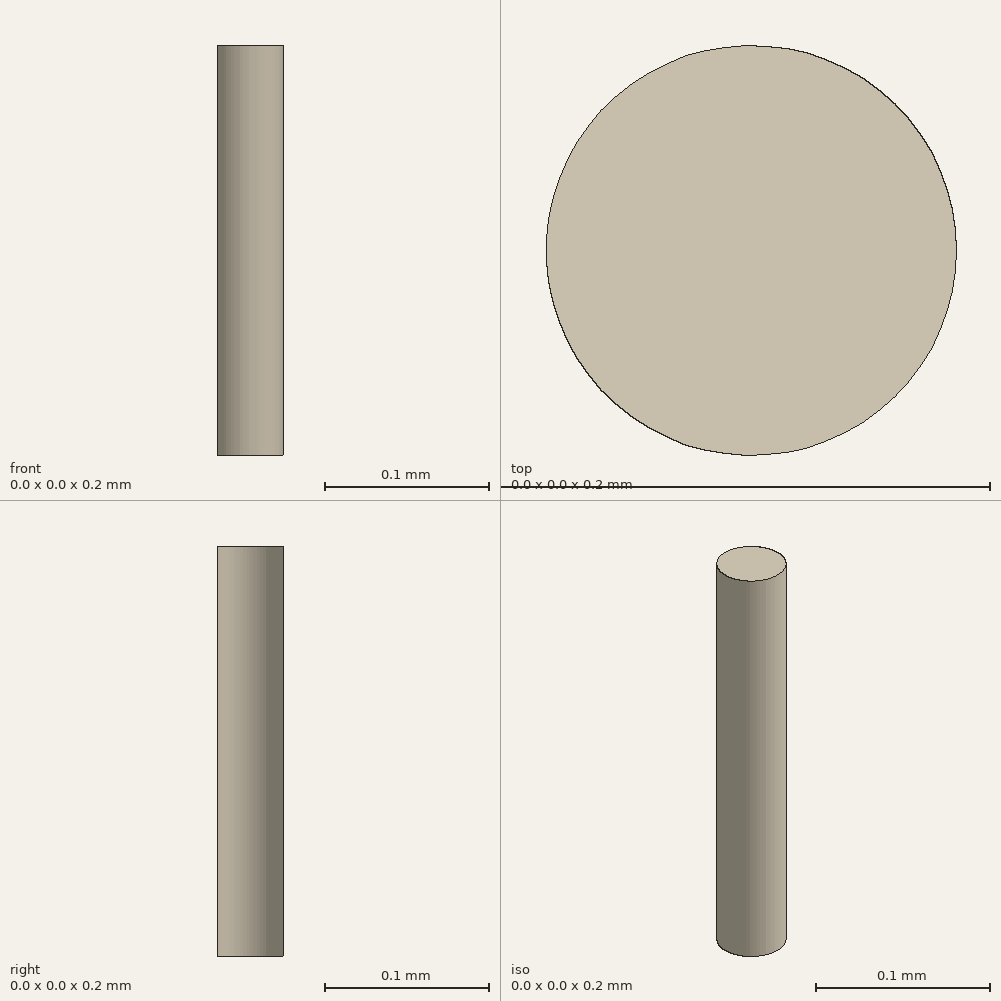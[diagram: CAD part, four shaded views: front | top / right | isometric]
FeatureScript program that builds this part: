
annotation { "Feature Type Name" : "Feature", "Feature Type Description" : "" }
export const myFeature = defineFeature(function(context is Context, id is Id, definition is map)
    precondition{}
    {
        {
            var Q0;
            Q0=qCreatedBy(makeId("Top.planeOp"),FACE);
            var sketch = newSketch(context, id + "F0", { "sketchPlane" : qUnion([Q0])});
            skCircle(sketch, "E0", {"center": v(24.22, -0.45) * mm, "radius": 0.02 * mm});
            skCircle(sketch, "E1", {"center": v(24.22, -0.6) * mm, "radius": 0.02 * mm});
            skCircle(sketch, "E2", {"center": v(24.22, -0.75) * mm, "radius": 0.02 * mm});
            skCircle(sketch, "E3", {"center": v(24.22, -0.3) * mm, "radius": 0.02 * mm});
            skCircle(sketch, "E4", {"center": v(24.22, 0.15) * mm, "radius": 0.02 * mm});
            skCircle(sketch, "E5", {"center": v(24.22, 0) * mm, "radius": 0.02 * mm});
            skCircle(sketch, "E6", {"center": v(24.22, -0.15) * mm, "radius": 0.02 * mm});
            skCircle(sketch, "E7", {"center": v(24.22, 0.75) * mm, "radius": 0.02 * mm});
            skCircle(sketch, "E8", {"center": v(24.22, 0.6) * mm, "radius": 0.02 * mm});
            skCircle(sketch, "E9", {"center": v(24.22, 0.45) * mm, "radius": 0.02 * mm});
            skCircle(sketch, "E10", {"center": v(24.22, 0.3) * mm, "radius": 0.02 * mm});
            skCircle(sketch, "E11", {"center": v(24.33, 0.83) * mm, "radius": 0.03 * mm});
            skCircle(sketch, "E12", {"center": v(24.42, 0.83) * mm, "radius": 0.03 * mm});
            skCircle(sketch, "E13", {"center": v(24.5, 0.83) * mm, "radius": 0.03 * mm});
            skCircle(sketch, "E14", {"center": v(24.59, 0.83) * mm, "radius": 0.03 * mm});
            skCircle(sketch, "E15", {"center": v(24.67, 0.83) * mm, "radius": 0.03 * mm});
            skCircle(sketch, "E16", {"center": v(24.76, 0.83) * mm, "radius": 0.03 * mm});
            skCircle(sketch, "E17", {"center": v(24.1, 0.83) * mm, "radius": 0.03 * mm});
            skCircle(sketch, "E18", {"center": v(24.18, 0.83) * mm, "radius": 0.03 * mm});
            skCircle(sketch, "E19", {"center": v(24.26, 0.83) * mm, "radius": 0.03 * mm});
            skCircle(sketch, "E20", {"center": v(25.3, 0.83) * mm, "radius": 0.03 * mm});
            skCircle(sketch, "E21", {"center": v(25.22, 0.83) * mm, "radius": 0.03 * mm});
            skCircle(sketch, "E22", {"center": v(25.14, 0.83) * mm, "radius": 0.03 * mm});
            skCircle(sketch, "E23", {"center": v(25.05, 0.83) * mm, "radius": 0.03 * mm});
            skCircle(sketch, "E24", {"center": v(24.97, 0.83) * mm, "radius": 0.03 * mm});
            skCircle(sketch, "E25", {"center": v(24.88, 0.83) * mm, "radius": 0.03 * mm});
            skCircle(sketch, "E26", {"center": v(25.53, 0.83) * mm, "radius": 0.03 * mm});
            skCircle(sketch, "E27", {"center": v(25.46, 0.83) * mm, "radius": 0.03 * mm});
            skCircle(sketch, "E28", {"center": v(25.38, 0.83) * mm, "radius": 0.03 * mm});
            skLineSegment(sketch, "E29", {"start": v(24.22, 0.88) * mm, "end": v(22.83, 0.88) * mm});
            skLineSegment(sketch, "E30", {"start": v(24.22, 0.92) * mm, "end": v(22.83, 0.92) * mm});
            skLineSegment(sketch, "E31", {"start": v(22.83, 0.92) * mm, "end": v(22.83, 0.88) * mm});
            skCircle(sketch, "E32", {"center": v(24.29, 0.75) * mm, "radius": 0.03 * mm});
            skCircle(sketch, "E33", {"center": v(24.37, 0.75) * mm, "radius": 0.03 * mm});
            skCircle(sketch, "E34", {"center": v(24.46, 0.75) * mm, "radius": 0.03 * mm});
            skCircle(sketch, "E35", {"center": v(24.54, 0.75) * mm, "radius": 0.03 * mm});
            skCircle(sketch, "E36", {"center": v(24.63, 0.75) * mm, "radius": 0.03 * mm});
            skCircle(sketch, "E37", {"center": v(24.71, 0.75) * mm, "radius": 0.03 * mm});
            skCircle(sketch, "E38", {"center": v(24.8, 0.75) * mm, "radius": 0.03 * mm});
            skCircle(sketch, "E39", {"center": v(24.33, 0.68) * mm, "radius": 0.03 * mm});
            skCircle(sketch, "E40", {"center": v(24.42, 0.68) * mm, "radius": 0.03 * mm});
            skCircle(sketch, "E41", {"center": v(24.5, 0.68) * mm, "radius": 0.03 * mm});
            skCircle(sketch, "E42", {"center": v(24.59, 0.68) * mm, "radius": 0.03 * mm});
            skCircle(sketch, "E43", {"center": v(24.67, 0.68) * mm, "radius": 0.03 * mm});
            skCircle(sketch, "E44", {"center": v(24.76, 0.68) * mm, "radius": 0.03 * mm});
            skCircle(sketch, "E45", {"center": v(24.1, 0.68) * mm, "radius": 0.03 * mm});
            skCircle(sketch, "E46", {"center": v(24.18, 0.68) * mm, "radius": 0.03 * mm});
            skCircle(sketch, "E47", {"center": v(24.26, 0.68) * mm, "radius": 0.03 * mm});
            skCircle(sketch, "E48", {"center": v(25.35, 0.75) * mm, "radius": 0.03 * mm});
            skCircle(sketch, "E49", {"center": v(25.26, 0.75) * mm, "radius": 0.03 * mm});
            skCircle(sketch, "E50", {"center": v(25.18, 0.75) * mm, "radius": 0.03 * mm});
            skCircle(sketch, "E51", {"center": v(25.1, 0.75) * mm, "radius": 0.03 * mm});
            skCircle(sketch, "E52", {"center": v(25, 0.75) * mm, "radius": 0.03 * mm});
            skCircle(sketch, "E53", {"center": v(24.92, 0.75) * mm, "radius": 0.03 * mm});
            skCircle(sketch, "E54", {"center": v(25.3, 0.68) * mm, "radius": 0.03 * mm});
            skCircle(sketch, "E55", {"center": v(25.22, 0.68) * mm, "radius": 0.03 * mm});
            skCircle(sketch, "E56", {"center": v(25.14, 0.68) * mm, "radius": 0.03 * mm});
            skCircle(sketch, "E57", {"center": v(25.05, 0.68) * mm, "radius": 0.03 * mm});
            skCircle(sketch, "E58", {"center": v(24.97, 0.68) * mm, "radius": 0.03 * mm});
            skCircle(sketch, "E59", {"center": v(24.88, 0.68) * mm, "radius": 0.03 * mm});
            skCircle(sketch, "E60", {"center": v(25.42, 0.75) * mm, "radius": 0.02 * mm});
            skCircle(sketch, "E61", {"center": v(25.53, 0.68) * mm, "radius": 0.03 * mm});
            skCircle(sketch, "E62", {"center": v(25.46, 0.68) * mm, "radius": 0.03 * mm});
            skCircle(sketch, "E63", {"center": v(25.38, 0.68) * mm, "radius": 0.03 * mm});
            skCircle(sketch, "E64", {"center": v(24.1, 0.75) * mm, "radius": 0.02 * mm});
            skCircle(sketch, "E65", {"center": v(24.16, 0.75) * mm, "radius": 0.02 * mm});
            skCircle(sketch, "E66", {"center": v(25.54, 0.75) * mm, "radius": 0.02 * mm});
            skCircle(sketch, "E67", {"center": v(25.48, 0.75) * mm, "radius": 0.02 * mm});
            skCircle(sketch, "E68", {"center": v(24.29, 0.6) * mm, "radius": 0.03 * mm});
            skCircle(sketch, "E69", {"center": v(24.37, 0.6) * mm, "radius": 0.03 * mm});
            skCircle(sketch, "E70", {"center": v(24.46, 0.6) * mm, "radius": 0.03 * mm});
            skCircle(sketch, "E71", {"center": v(24.54, 0.6) * mm, "radius": 0.03 * mm});
            skCircle(sketch, "E72", {"center": v(24.63, 0.6) * mm, "radius": 0.03 * mm});
            skCircle(sketch, "E73", {"center": v(24.71, 0.6) * mm, "radius": 0.03 * mm});
            skCircle(sketch, "E74", {"center": v(24.8, 0.6) * mm, "radius": 0.03 * mm});
            skCircle(sketch, "E75", {"center": v(24.33, 0.52) * mm, "radius": 0.03 * mm});
            skCircle(sketch, "E76", {"center": v(24.42, 0.52) * mm, "radius": 0.03 * mm});
            skCircle(sketch, "E77", {"center": v(24.5, 0.52) * mm, "radius": 0.03 * mm});
            skCircle(sketch, "E78", {"center": v(24.59, 0.52) * mm, "radius": 0.03 * mm});
            skCircle(sketch, "E79", {"center": v(24.67, 0.52) * mm, "radius": 0.03 * mm});
            skCircle(sketch, "E80", {"center": v(24.76, 0.52) * mm, "radius": 0.03 * mm});
            skCircle(sketch, "E81", {"center": v(24.1, 0.52) * mm, "radius": 0.03 * mm});
            skCircle(sketch, "E82", {"center": v(24.18, 0.52) * mm, "radius": 0.03 * mm});
            skCircle(sketch, "E83", {"center": v(24.26, 0.52) * mm, "radius": 0.03 * mm});
            skCircle(sketch, "E84", {"center": v(25.35, 0.6) * mm, "radius": 0.03 * mm});
            skCircle(sketch, "E85", {"center": v(25.26, 0.6) * mm, "radius": 0.03 * mm});
            skCircle(sketch, "E86", {"center": v(25.18, 0.6) * mm, "radius": 0.03 * mm});
            skCircle(sketch, "E87", {"center": v(25.1, 0.6) * mm, "radius": 0.03 * mm});
            skCircle(sketch, "E88", {"center": v(25, 0.6) * mm, "radius": 0.03 * mm});
            skCircle(sketch, "E89", {"center": v(24.92, 0.6) * mm, "radius": 0.03 * mm});
            skCircle(sketch, "E90", {"center": v(25.3, 0.52) * mm, "radius": 0.03 * mm});
            skCircle(sketch, "E91", {"center": v(25.22, 0.52) * mm, "radius": 0.03 * mm});
            skCircle(sketch, "E92", {"center": v(25.14, 0.52) * mm, "radius": 0.03 * mm});
            skCircle(sketch, "E93", {"center": v(25.05, 0.52) * mm, "radius": 0.03 * mm});
            skCircle(sketch, "E94", {"center": v(24.97, 0.52) * mm, "radius": 0.03 * mm});
            skCircle(sketch, "E95", {"center": v(24.88, 0.52) * mm, "radius": 0.03 * mm});
            skCircle(sketch, "E96", {"center": v(25.42, 0.6) * mm, "radius": 0.02 * mm});
            skCircle(sketch, "E97", {"center": v(25.53, 0.52) * mm, "radius": 0.03 * mm});
            skCircle(sketch, "E98", {"center": v(25.46, 0.52) * mm, "radius": 0.03 * mm});
            skCircle(sketch, "E99", {"center": v(25.38, 0.52) * mm, "radius": 0.03 * mm});
            skCircle(sketch, "E100", {"center": v(24.1, 0.6) * mm, "radius": 0.02 * mm});
            skCircle(sketch, "E101", {"center": v(24.16, 0.6) * mm, "radius": 0.02 * mm});
            skCircle(sketch, "E102", {"center": v(25.54, 0.6) * mm, "radius": 0.02 * mm});
            skCircle(sketch, "E103", {"center": v(25.48, 0.6) * mm, "radius": 0.02 * mm});
            skCircle(sketch, "E104", {"center": v(24.29, 0.45) * mm, "radius": 0.03 * mm});
            skCircle(sketch, "E105", {"center": v(24.37, 0.45) * mm, "radius": 0.03 * mm});
            skCircle(sketch, "E106", {"center": v(24.46, 0.45) * mm, "radius": 0.03 * mm});
            skCircle(sketch, "E107", {"center": v(24.54, 0.45) * mm, "radius": 0.03 * mm});
            skCircle(sketch, "E108", {"center": v(24.63, 0.45) * mm, "radius": 0.03 * mm});
            skCircle(sketch, "E109", {"center": v(24.71, 0.45) * mm, "radius": 0.03 * mm});
            skCircle(sketch, "E110", {"center": v(24.8, 0.45) * mm, "radius": 0.03 * mm});
            skCircle(sketch, "E111", {"center": v(24.33, 0.38) * mm, "radius": 0.03 * mm});
            skCircle(sketch, "E112", {"center": v(24.42, 0.38) * mm, "radius": 0.03 * mm});
            skCircle(sketch, "E113", {"center": v(24.5, 0.38) * mm, "radius": 0.03 * mm});
            skCircle(sketch, "E114", {"center": v(24.59, 0.38) * mm, "radius": 0.03 * mm});
            skCircle(sketch, "E115", {"center": v(24.67, 0.38) * mm, "radius": 0.03 * mm});
            skCircle(sketch, "E116", {"center": v(24.76, 0.38) * mm, "radius": 0.03 * mm});
            skCircle(sketch, "E117", {"center": v(24.1, 0.38) * mm, "radius": 0.03 * mm});
            skCircle(sketch, "E118", {"center": v(24.18, 0.38) * mm, "radius": 0.03 * mm});
            skCircle(sketch, "E119", {"center": v(24.26, 0.38) * mm, "radius": 0.03 * mm});
            skCircle(sketch, "E120", {"center": v(25.35, 0.45) * mm, "radius": 0.03 * mm});
            skCircle(sketch, "E121", {"center": v(25.26, 0.45) * mm, "radius": 0.03 * mm});
            skCircle(sketch, "E122", {"center": v(25.18, 0.45) * mm, "radius": 0.03 * mm});
            skCircle(sketch, "E123", {"center": v(25.1, 0.45) * mm, "radius": 0.03 * mm});
            skCircle(sketch, "E124", {"center": v(25, 0.45) * mm, "radius": 0.03 * mm});
            skCircle(sketch, "E125", {"center": v(24.92, 0.45) * mm, "radius": 0.03 * mm});
            skCircle(sketch, "E126", {"center": v(25.3, 0.38) * mm, "radius": 0.03 * mm});
            skCircle(sketch, "E127", {"center": v(25.22, 0.38) * mm, "radius": 0.03 * mm});
            skCircle(sketch, "E128", {"center": v(25.14, 0.38) * mm, "radius": 0.03 * mm});
            skCircle(sketch, "E129", {"center": v(25.05, 0.38) * mm, "radius": 0.03 * mm});
            skCircle(sketch, "E130", {"center": v(24.97, 0.38) * mm, "radius": 0.03 * mm});
            skCircle(sketch, "E131", {"center": v(24.88, 0.38) * mm, "radius": 0.03 * mm});
            skCircle(sketch, "E132", {"center": v(25.42, 0.45) * mm, "radius": 0.02 * mm});
            skCircle(sketch, "E133", {"center": v(25.53, 0.38) * mm, "radius": 0.03 * mm});
            skCircle(sketch, "E134", {"center": v(25.46, 0.38) * mm, "radius": 0.03 * mm});
            skCircle(sketch, "E135", {"center": v(25.38, 0.38) * mm, "radius": 0.03 * mm});
            skCircle(sketch, "E136", {"center": v(24.1, 0.45) * mm, "radius": 0.02 * mm});
            skCircle(sketch, "E137", {"center": v(24.16, 0.45) * mm, "radius": 0.02 * mm});
            skCircle(sketch, "E138", {"center": v(25.54, 0.45) * mm, "radius": 0.02 * mm});
            skCircle(sketch, "E139", {"center": v(25.48, 0.45) * mm, "radius": 0.02 * mm});
            skCircle(sketch, "E140", {"center": v(24.29, 0.3) * mm, "radius": 0.03 * mm});
            skCircle(sketch, "E141", {"center": v(24.37, 0.3) * mm, "radius": 0.03 * mm});
            skCircle(sketch, "E142", {"center": v(24.46, 0.3) * mm, "radius": 0.03 * mm});
            skCircle(sketch, "E143", {"center": v(24.54, 0.3) * mm, "radius": 0.03 * mm});
            skCircle(sketch, "E144", {"center": v(24.63, 0.3) * mm, "radius": 0.03 * mm});
            skCircle(sketch, "E145", {"center": v(24.71, 0.3) * mm, "radius": 0.03 * mm});
            skCircle(sketch, "E146", {"center": v(24.8, 0.3) * mm, "radius": 0.03 * mm});
            skCircle(sketch, "E147", {"center": v(24.33, 0.23) * mm, "radius": 0.03 * mm});
            skCircle(sketch, "E148", {"center": v(24.42, 0.23) * mm, "radius": 0.03 * mm});
            skCircle(sketch, "E149", {"center": v(24.5, 0.23) * mm, "radius": 0.03 * mm});
            skCircle(sketch, "E150", {"center": v(24.59, 0.23) * mm, "radius": 0.03 * mm});
            skCircle(sketch, "E151", {"center": v(24.67, 0.23) * mm, "radius": 0.03 * mm});
            skCircle(sketch, "E152", {"center": v(24.76, 0.23) * mm, "radius": 0.03 * mm});
            skCircle(sketch, "E153", {"center": v(24.1, 0.23) * mm, "radius": 0.03 * mm});
            skCircle(sketch, "E154", {"center": v(24.18, 0.23) * mm, "radius": 0.03 * mm});
            skCircle(sketch, "E155", {"center": v(24.26, 0.23) * mm, "radius": 0.03 * mm});
            skCircle(sketch, "E156", {"center": v(25.35, 0.3) * mm, "radius": 0.03 * mm});
            skCircle(sketch, "E157", {"center": v(25.26, 0.3) * mm, "radius": 0.03 * mm});
            skCircle(sketch, "E158", {"center": v(25.18, 0.3) * mm, "radius": 0.03 * mm});
            skCircle(sketch, "E159", {"center": v(25.1, 0.3) * mm, "radius": 0.03 * mm});
            skCircle(sketch, "E160", {"center": v(25, 0.3) * mm, "radius": 0.03 * mm});
            skCircle(sketch, "E161", {"center": v(24.92, 0.3) * mm, "radius": 0.03 * mm});
            skCircle(sketch, "E162", {"center": v(25.3, 0.23) * mm, "radius": 0.03 * mm});
            skCircle(sketch, "E163", {"center": v(25.22, 0.23) * mm, "radius": 0.03 * mm});
            skCircle(sketch, "E164", {"center": v(25.14, 0.23) * mm, "radius": 0.03 * mm});
            skCircle(sketch, "E165", {"center": v(25.05, 0.23) * mm, "radius": 0.03 * mm});
            skCircle(sketch, "E166", {"center": v(24.97, 0.23) * mm, "radius": 0.03 * mm});
            skCircle(sketch, "E167", {"center": v(24.88, 0.23) * mm, "radius": 0.03 * mm});
            skCircle(sketch, "E168", {"center": v(25.42, 0.3) * mm, "radius": 0.02 * mm});
            skCircle(sketch, "E169", {"center": v(25.53, 0.23) * mm, "radius": 0.03 * mm});
            skCircle(sketch, "E170", {"center": v(25.46, 0.23) * mm, "radius": 0.03 * mm});
            skCircle(sketch, "E171", {"center": v(25.38, 0.23) * mm, "radius": 0.03 * mm});
            skCircle(sketch, "E172", {"center": v(24.1, 0.3) * mm, "radius": 0.02 * mm});
            skCircle(sketch, "E173", {"center": v(24.16, 0.3) * mm, "radius": 0.02 * mm});
            skCircle(sketch, "E174", {"center": v(25.54, 0.3) * mm, "radius": 0.02 * mm});
            skCircle(sketch, "E175", {"center": v(25.48, 0.3) * mm, "radius": 0.02 * mm});
            skCircle(sketch, "E176", {"center": v(24.29, 0.15) * mm, "radius": 0.03 * mm});
            skCircle(sketch, "E177", {"center": v(24.37, 0.15) * mm, "radius": 0.03 * mm});
            skCircle(sketch, "E178", {"center": v(24.46, 0.15) * mm, "radius": 0.03 * mm});
            skCircle(sketch, "E179", {"center": v(24.54, 0.15) * mm, "radius": 0.03 * mm});
            skCircle(sketch, "E180", {"center": v(24.63, 0.15) * mm, "radius": 0.03 * mm});
            skCircle(sketch, "E181", {"center": v(24.71, 0.15) * mm, "radius": 0.03 * mm});
            skCircle(sketch, "E182", {"center": v(24.8, 0.15) * mm, "radius": 0.03 * mm});
            skCircle(sketch, "E183", {"center": v(24.33, 0.08) * mm, "radius": 0.03 * mm});
            skCircle(sketch, "E184", {"center": v(24.42, 0.08) * mm, "radius": 0.03 * mm});
            skCircle(sketch, "E185", {"center": v(24.5, 0.08) * mm, "radius": 0.03 * mm});
            skCircle(sketch, "E186", {"center": v(24.59, 0.08) * mm, "radius": 0.03 * mm});
            skCircle(sketch, "E187", {"center": v(24.67, 0.08) * mm, "radius": 0.03 * mm});
            skCircle(sketch, "E188", {"center": v(24.76, 0.08) * mm, "radius": 0.03 * mm});
            skCircle(sketch, "E189", {"center": v(24.1, 0.08) * mm, "radius": 0.03 * mm});
            skCircle(sketch, "E190", {"center": v(24.18, 0.08) * mm, "radius": 0.03 * mm});
            skCircle(sketch, "E191", {"center": v(24.26, 0.08) * mm, "radius": 0.03 * mm});
            skCircle(sketch, "E192", {"center": v(25.35, 0.15) * mm, "radius": 0.03 * mm});
            skCircle(sketch, "E193", {"center": v(25.26, 0.15) * mm, "radius": 0.03 * mm});
            skCircle(sketch, "E194", {"center": v(25.18, 0.15) * mm, "radius": 0.03 * mm});
            skCircle(sketch, "E195", {"center": v(25.1, 0.15) * mm, "radius": 0.03 * mm});
            skCircle(sketch, "E196", {"center": v(25, 0.15) * mm, "radius": 0.03 * mm});
            skCircle(sketch, "E197", {"center": v(24.92, 0.15) * mm, "radius": 0.03 * mm});
            skCircle(sketch, "E198", {"center": v(25.3, 0.08) * mm, "radius": 0.03 * mm});
            skCircle(sketch, "E199", {"center": v(25.22, 0.08) * mm, "radius": 0.03 * mm});
            skCircle(sketch, "E200", {"center": v(25.14, 0.08) * mm, "radius": 0.03 * mm});
            skCircle(sketch, "E201", {"center": v(25.05, 0.08) * mm, "radius": 0.03 * mm});
            skCircle(sketch, "E202", {"center": v(24.97, 0.08) * mm, "radius": 0.03 * mm});
            skCircle(sketch, "E203", {"center": v(24.88, 0.08) * mm, "radius": 0.03 * mm});
            skCircle(sketch, "E204", {"center": v(25.42, 0.15) * mm, "radius": 0.02 * mm});
            skCircle(sketch, "E205", {"center": v(25.53, 0.08) * mm, "radius": 0.03 * mm});
            skCircle(sketch, "E206", {"center": v(25.46, 0.08) * mm, "radius": 0.03 * mm});
            skCircle(sketch, "E207", {"center": v(25.38, 0.08) * mm, "radius": 0.03 * mm});
            skCircle(sketch, "E208", {"center": v(24.1, 0.15) * mm, "radius": 0.02 * mm});
            skCircle(sketch, "E209", {"center": v(24.16, 0.15) * mm, "radius": 0.02 * mm});
            skCircle(sketch, "E210", {"center": v(25.54, 0.15) * mm, "radius": 0.02 * mm});
            skCircle(sketch, "E211", {"center": v(25.48, 0.15) * mm, "radius": 0.02 * mm});
            skCircle(sketch, "E212", {"center": v(24.29, 0) * mm, "radius": 0.03 * mm});
            skCircle(sketch, "E213", {"center": v(24.37, 0) * mm, "radius": 0.03 * mm});
            skCircle(sketch, "E214", {"center": v(24.46, 0) * mm, "radius": 0.03 * mm});
            skCircle(sketch, "E215", {"center": v(24.54, 0) * mm, "radius": 0.03 * mm});
            skCircle(sketch, "E216", {"center": v(24.63, 0) * mm, "radius": 0.03 * mm});
            skCircle(sketch, "E217", {"center": v(24.71, 0) * mm, "radius": 0.03 * mm});
            skCircle(sketch, "E218", {"center": v(24.8, 0) * mm, "radius": 0.03 * mm});
            skCircle(sketch, "E219", {"center": v(24.33, -0.07) * mm, "radius": 0.03 * mm});
            skCircle(sketch, "E220", {"center": v(24.42, -0.07) * mm, "radius": 0.03 * mm});
            skCircle(sketch, "E221", {"center": v(24.5, -0.07) * mm, "radius": 0.03 * mm});
            skCircle(sketch, "E222", {"center": v(24.59, -0.07) * mm, "radius": 0.03 * mm});
            skCircle(sketch, "E223", {"center": v(24.67, -0.07) * mm, "radius": 0.03 * mm});
            skCircle(sketch, "E224", {"center": v(24.76, -0.07) * mm, "radius": 0.03 * mm});
            skCircle(sketch, "E225", {"center": v(24.1, -0.07) * mm, "radius": 0.03 * mm});
            skCircle(sketch, "E226", {"center": v(24.18, -0.07) * mm, "radius": 0.03 * mm});
            skCircle(sketch, "E227", {"center": v(24.26, -0.07) * mm, "radius": 0.03 * mm});
            skCircle(sketch, "E228", {"center": v(25.35, 0) * mm, "radius": 0.03 * mm});
            skCircle(sketch, "E229", {"center": v(25.26, 0) * mm, "radius": 0.03 * mm});
            skCircle(sketch, "E230", {"center": v(25.18, 0) * mm, "radius": 0.03 * mm});
            skCircle(sketch, "E231", {"center": v(25.1, 0) * mm, "radius": 0.03 * mm});
            skCircle(sketch, "E232", {"center": v(25, 0) * mm, "radius": 0.03 * mm});
            skCircle(sketch, "E233", {"center": v(24.92, 0) * mm, "radius": 0.03 * mm});
            skCircle(sketch, "E234", {"center": v(25.3, -0.07) * mm, "radius": 0.03 * mm});
            skCircle(sketch, "E235", {"center": v(25.22, -0.07) * mm, "radius": 0.03 * mm});
            skCircle(sketch, "E236", {"center": v(25.14, -0.07) * mm, "radius": 0.03 * mm});
            skCircle(sketch, "E237", {"center": v(25.05, -0.07) * mm, "radius": 0.03 * mm});
            skCircle(sketch, "E238", {"center": v(24.97, -0.07) * mm, "radius": 0.03 * mm});
            skCircle(sketch, "E239", {"center": v(24.88, -0.07) * mm, "radius": 0.03 * mm});
            skCircle(sketch, "E240", {"center": v(25.42, 0) * mm, "radius": 0.02 * mm});
            skCircle(sketch, "E241", {"center": v(25.53, -0.07) * mm, "radius": 0.03 * mm});
            skCircle(sketch, "E242", {"center": v(25.46, -0.07) * mm, "radius": 0.03 * mm});
            skCircle(sketch, "E243", {"center": v(25.38, -0.07) * mm, "radius": 0.03 * mm});
            skCircle(sketch, "E244", {"center": v(24.1, 0) * mm, "radius": 0.02 * mm});
            skCircle(sketch, "E245", {"center": v(24.16, 0) * mm, "radius": 0.02 * mm});
            skCircle(sketch, "E246", {"center": v(25.54, 0) * mm, "radius": 0.02 * mm});
            skCircle(sketch, "E247", {"center": v(25.48, 0) * mm, "radius": 0.02 * mm});
            skCircle(sketch, "E248", {"center": v(24.29, -0.15) * mm, "radius": 0.03 * mm});
            skCircle(sketch, "E249", {"center": v(24.37, -0.15) * mm, "radius": 0.03 * mm});
            skCircle(sketch, "E250", {"center": v(24.46, -0.15) * mm, "radius": 0.03 * mm});
            skCircle(sketch, "E251", {"center": v(24.54, -0.15) * mm, "radius": 0.03 * mm});
            skCircle(sketch, "E252", {"center": v(24.63, -0.15) * mm, "radius": 0.03 * mm});
            skCircle(sketch, "E253", {"center": v(24.71, -0.15) * mm, "radius": 0.03 * mm});
            skCircle(sketch, "E254", {"center": v(24.8, -0.15) * mm, "radius": 0.03 * mm});
            skCircle(sketch, "E255", {"center": v(24.33, -0.23) * mm, "radius": 0.03 * mm});
            skCircle(sketch, "E256", {"center": v(24.42, -0.23) * mm, "radius": 0.03 * mm});
            skCircle(sketch, "E257", {"center": v(24.5, -0.23) * mm, "radius": 0.03 * mm});
            skCircle(sketch, "E258", {"center": v(24.59, -0.23) * mm, "radius": 0.03 * mm});
            skCircle(sketch, "E259", {"center": v(24.67, -0.23) * mm, "radius": 0.03 * mm});
            skCircle(sketch, "E260", {"center": v(24.76, -0.23) * mm, "radius": 0.03 * mm});
            skCircle(sketch, "E261", {"center": v(24.1, -0.23) * mm, "radius": 0.03 * mm});
            skCircle(sketch, "E262", {"center": v(24.18, -0.23) * mm, "radius": 0.03 * mm});
            skCircle(sketch, "E263", {"center": v(24.26, -0.23) * mm, "radius": 0.03 * mm});
            skCircle(sketch, "E264", {"center": v(25.35, -0.15) * mm, "radius": 0.03 * mm});
            skCircle(sketch, "E265", {"center": v(25.26, -0.15) * mm, "radius": 0.03 * mm});
            skCircle(sketch, "E266", {"center": v(25.18, -0.15) * mm, "radius": 0.03 * mm});
            skCircle(sketch, "E267", {"center": v(25.1, -0.15) * mm, "radius": 0.03 * mm});
            skCircle(sketch, "E268", {"center": v(25, -0.15) * mm, "radius": 0.03 * mm});
            skCircle(sketch, "E269", {"center": v(24.92, -0.15) * mm, "radius": 0.03 * mm});
            skCircle(sketch, "E270", {"center": v(25.3, -0.23) * mm, "radius": 0.03 * mm});
            skCircle(sketch, "E271", {"center": v(25.22, -0.23) * mm, "radius": 0.03 * mm});
            skCircle(sketch, "E272", {"center": v(25.14, -0.23) * mm, "radius": 0.03 * mm});
            skCircle(sketch, "E273", {"center": v(25.05, -0.23) * mm, "radius": 0.03 * mm});
            skCircle(sketch, "E274", {"center": v(24.97, -0.23) * mm, "radius": 0.03 * mm});
            skCircle(sketch, "E275", {"center": v(24.88, -0.23) * mm, "radius": 0.03 * mm});
            skCircle(sketch, "E276", {"center": v(25.42, -0.15) * mm, "radius": 0.02 * mm});
            skCircle(sketch, "E277", {"center": v(25.53, -0.23) * mm, "radius": 0.03 * mm});
            skCircle(sketch, "E278", {"center": v(25.46, -0.23) * mm, "radius": 0.03 * mm});
            skCircle(sketch, "E279", {"center": v(25.38, -0.23) * mm, "radius": 0.03 * mm});
            skCircle(sketch, "E280", {"center": v(24.1, -0.15) * mm, "radius": 0.02 * mm});
            skCircle(sketch, "E281", {"center": v(24.16, -0.15) * mm, "radius": 0.02 * mm});
            skCircle(sketch, "E282", {"center": v(25.54, -0.15) * mm, "radius": 0.02 * mm});
            skCircle(sketch, "E283", {"center": v(25.48, -0.15) * mm, "radius": 0.02 * mm});
            skCircle(sketch, "E284", {"center": v(24.29, -0.3) * mm, "radius": 0.03 * mm});
            skCircle(sketch, "E285", {"center": v(24.37, -0.3) * mm, "radius": 0.03 * mm});
            skCircle(sketch, "E286", {"center": v(24.46, -0.3) * mm, "radius": 0.03 * mm});
            skCircle(sketch, "E287", {"center": v(24.54, -0.3) * mm, "radius": 0.03 * mm});
            skCircle(sketch, "E288", {"center": v(24.63, -0.3) * mm, "radius": 0.03 * mm});
            skCircle(sketch, "E289", {"center": v(24.71, -0.3) * mm, "radius": 0.03 * mm});
            skCircle(sketch, "E290", {"center": v(24.8, -0.3) * mm, "radius": 0.03 * mm});
            skCircle(sketch, "E291", {"center": v(24.33, -0.38) * mm, "radius": 0.03 * mm});
            skCircle(sketch, "E292", {"center": v(24.42, -0.38) * mm, "radius": 0.03 * mm});
            skCircle(sketch, "E293", {"center": v(24.5, -0.38) * mm, "radius": 0.03 * mm});
            skCircle(sketch, "E294", {"center": v(24.59, -0.38) * mm, "radius": 0.03 * mm});
            skCircle(sketch, "E295", {"center": v(24.67, -0.38) * mm, "radius": 0.03 * mm});
            skCircle(sketch, "E296", {"center": v(24.76, -0.38) * mm, "radius": 0.03 * mm});
            skCircle(sketch, "E297", {"center": v(24.1, -0.38) * mm, "radius": 0.03 * mm});
            skCircle(sketch, "E298", {"center": v(24.18, -0.38) * mm, "radius": 0.03 * mm});
            skCircle(sketch, "E299", {"center": v(24.26, -0.38) * mm, "radius": 0.03 * mm});
            skCircle(sketch, "E300", {"center": v(25.35, -0.3) * mm, "radius": 0.03 * mm});
            skCircle(sketch, "E301", {"center": v(25.26, -0.3) * mm, "radius": 0.03 * mm});
            skCircle(sketch, "E302", {"center": v(25.18, -0.3) * mm, "radius": 0.03 * mm});
            skCircle(sketch, "E303", {"center": v(25.1, -0.3) * mm, "radius": 0.03 * mm});
            skCircle(sketch, "E304", {"center": v(25, -0.3) * mm, "radius": 0.03 * mm});
            skCircle(sketch, "E305", {"center": v(24.92, -0.3) * mm, "radius": 0.03 * mm});
            skCircle(sketch, "E306", {"center": v(25.3, -0.38) * mm, "radius": 0.03 * mm});
            skCircle(sketch, "E307", {"center": v(25.22, -0.38) * mm, "radius": 0.03 * mm});
            skCircle(sketch, "E308", {"center": v(25.14, -0.38) * mm, "radius": 0.03 * mm});
            skCircle(sketch, "E309", {"center": v(25.05, -0.38) * mm, "radius": 0.03 * mm});
            skCircle(sketch, "E310", {"center": v(24.97, -0.38) * mm, "radius": 0.03 * mm});
            skCircle(sketch, "E311", {"center": v(24.88, -0.38) * mm, "radius": 0.03 * mm});
            skCircle(sketch, "E312", {"center": v(25.42, -0.3) * mm, "radius": 0.02 * mm});
            skCircle(sketch, "E313", {"center": v(25.53, -0.38) * mm, "radius": 0.03 * mm});
            skCircle(sketch, "E314", {"center": v(25.46, -0.38) * mm, "radius": 0.03 * mm});
            skCircle(sketch, "E315", {"center": v(25.38, -0.38) * mm, "radius": 0.03 * mm});
            skCircle(sketch, "E316", {"center": v(24.1, -0.3) * mm, "radius": 0.02 * mm});
            skCircle(sketch, "E317", {"center": v(24.16, -0.3) * mm, "radius": 0.02 * mm});
            skCircle(sketch, "E318", {"center": v(25.54, -0.3) * mm, "radius": 0.02 * mm});
            skCircle(sketch, "E319", {"center": v(25.48, -0.3) * mm, "radius": 0.02 * mm});
            skCircle(sketch, "E320", {"center": v(24.29, -0.45) * mm, "radius": 0.03 * mm});
            skCircle(sketch, "E321", {"center": v(24.37, -0.45) * mm, "radius": 0.03 * mm});
            skCircle(sketch, "E322", {"center": v(24.46, -0.45) * mm, "radius": 0.03 * mm});
            skCircle(sketch, "E323", {"center": v(24.54, -0.45) * mm, "radius": 0.03 * mm});
            skCircle(sketch, "E324", {"center": v(24.63, -0.45) * mm, "radius": 0.03 * mm});
            skCircle(sketch, "E325", {"center": v(24.71, -0.45) * mm, "radius": 0.03 * mm});
            skCircle(sketch, "E326", {"center": v(24.8, -0.45) * mm, "radius": 0.03 * mm});
            skCircle(sketch, "E327", {"center": v(24.33, -0.52) * mm, "radius": 0.03 * mm});
            skCircle(sketch, "E328", {"center": v(24.42, -0.52) * mm, "radius": 0.03 * mm});
            skCircle(sketch, "E329", {"center": v(24.5, -0.52) * mm, "radius": 0.03 * mm});
            skCircle(sketch, "E330", {"center": v(24.59, -0.52) * mm, "radius": 0.03 * mm});
            skCircle(sketch, "E331", {"center": v(24.67, -0.52) * mm, "radius": 0.03 * mm});
            skCircle(sketch, "E332", {"center": v(24.76, -0.52) * mm, "radius": 0.03 * mm});
            skCircle(sketch, "E333", {"center": v(24.1, -0.52) * mm, "radius": 0.03 * mm});
            skCircle(sketch, "E334", {"center": v(24.18, -0.52) * mm, "radius": 0.03 * mm});
            skCircle(sketch, "E335", {"center": v(24.26, -0.52) * mm, "radius": 0.03 * mm});
            skCircle(sketch, "E336", {"center": v(25.35, -0.45) * mm, "radius": 0.03 * mm});
            skCircle(sketch, "E337", {"center": v(25.26, -0.45) * mm, "radius": 0.03 * mm});
            skCircle(sketch, "E338", {"center": v(25.18, -0.45) * mm, "radius": 0.03 * mm});
            skCircle(sketch, "E339", {"center": v(25.1, -0.45) * mm, "radius": 0.03 * mm});
            skCircle(sketch, "E340", {"center": v(25, -0.45) * mm, "radius": 0.03 * mm});
            skCircle(sketch, "E341", {"center": v(24.92, -0.45) * mm, "radius": 0.03 * mm});
            skCircle(sketch, "E342", {"center": v(25.3, -0.52) * mm, "radius": 0.03 * mm});
            skCircle(sketch, "E343", {"center": v(25.22, -0.52) * mm, "radius": 0.03 * mm});
            skCircle(sketch, "E344", {"center": v(25.14, -0.52) * mm, "radius": 0.03 * mm});
            skCircle(sketch, "E345", {"center": v(25.05, -0.52) * mm, "radius": 0.03 * mm});
            skCircle(sketch, "E346", {"center": v(24.97, -0.52) * mm, "radius": 0.03 * mm});
            skCircle(sketch, "E347", {"center": v(24.88, -0.52) * mm, "radius": 0.03 * mm});
            skCircle(sketch, "E348", {"center": v(25.42, -0.45) * mm, "radius": 0.02 * mm});
            skCircle(sketch, "E349", {"center": v(25.53, -0.52) * mm, "radius": 0.03 * mm});
            skCircle(sketch, "E350", {"center": v(25.46, -0.52) * mm, "radius": 0.03 * mm});
            skCircle(sketch, "E351", {"center": v(25.38, -0.52) * mm, "radius": 0.03 * mm});
            skCircle(sketch, "E352", {"center": v(24.1, -0.45) * mm, "radius": 0.02 * mm});
            skCircle(sketch, "E353", {"center": v(24.16, -0.45) * mm, "radius": 0.02 * mm});
            skCircle(sketch, "E354", {"center": v(25.54, -0.45) * mm, "radius": 0.02 * mm});
            skCircle(sketch, "E355", {"center": v(25.48, -0.45) * mm, "radius": 0.02 * mm});
            skCircle(sketch, "E356", {"center": v(24.29, -0.6) * mm, "radius": 0.03 * mm});
            skCircle(sketch, "E357", {"center": v(24.37, -0.6) * mm, "radius": 0.03 * mm});
            skCircle(sketch, "E358", {"center": v(24.46, -0.6) * mm, "radius": 0.03 * mm});
            skCircle(sketch, "E359", {"center": v(24.54, -0.6) * mm, "radius": 0.03 * mm});
            skCircle(sketch, "E360", {"center": v(24.63, -0.6) * mm, "radius": 0.03 * mm});
            skCircle(sketch, "E361", {"center": v(24.71, -0.6) * mm, "radius": 0.03 * mm});
            skCircle(sketch, "E362", {"center": v(24.8, -0.6) * mm, "radius": 0.03 * mm});
            skCircle(sketch, "E363", {"center": v(24.33, -0.67) * mm, "radius": 0.03 * mm});
            skCircle(sketch, "E364", {"center": v(24.42, -0.67) * mm, "radius": 0.03 * mm});
            skCircle(sketch, "E365", {"center": v(24.5, -0.67) * mm, "radius": 0.03 * mm});
            skCircle(sketch, "E366", {"center": v(24.59, -0.67) * mm, "radius": 0.03 * mm});
            skCircle(sketch, "E367", {"center": v(24.67, -0.67) * mm, "radius": 0.03 * mm});
            skCircle(sketch, "E368", {"center": v(24.76, -0.67) * mm, "radius": 0.03 * mm});
            skCircle(sketch, "E369", {"center": v(24.1, -0.67) * mm, "radius": 0.03 * mm});
            skCircle(sketch, "E370", {"center": v(24.18, -0.67) * mm, "radius": 0.03 * mm});
            skCircle(sketch, "E371", {"center": v(24.26, -0.67) * mm, "radius": 0.03 * mm});
            skCircle(sketch, "E372", {"center": v(25.35, -0.6) * mm, "radius": 0.03 * mm});
            skCircle(sketch, "E373", {"center": v(25.26, -0.6) * mm, "radius": 0.03 * mm});
            skCircle(sketch, "E374", {"center": v(25.18, -0.6) * mm, "radius": 0.03 * mm});
            skCircle(sketch, "E375", {"center": v(25.1, -0.6) * mm, "radius": 0.03 * mm});
            skCircle(sketch, "E376", {"center": v(25, -0.6) * mm, "radius": 0.03 * mm});
            skCircle(sketch, "E377", {"center": v(24.92, -0.6) * mm, "radius": 0.03 * mm});
            skCircle(sketch, "E378", {"center": v(25.3, -0.67) * mm, "radius": 0.03 * mm});
            skCircle(sketch, "E379", {"center": v(25.22, -0.67) * mm, "radius": 0.03 * mm});
            skCircle(sketch, "E380", {"center": v(25.14, -0.67) * mm, "radius": 0.03 * mm});
            skCircle(sketch, "E381", {"center": v(25.05, -0.67) * mm, "radius": 0.03 * mm});
            skCircle(sketch, "E382", {"center": v(24.97, -0.67) * mm, "radius": 0.03 * mm});
            skCircle(sketch, "E383", {"center": v(24.88, -0.67) * mm, "radius": 0.03 * mm});
            skCircle(sketch, "E384", {"center": v(25.42, -0.6) * mm, "radius": 0.02 * mm});
            skCircle(sketch, "E385", {"center": v(25.53, -0.67) * mm, "radius": 0.03 * mm});
            skCircle(sketch, "E386", {"center": v(25.46, -0.67) * mm, "radius": 0.03 * mm});
            skCircle(sketch, "E387", {"center": v(25.38, -0.67) * mm, "radius": 0.03 * mm});
            skCircle(sketch, "E388", {"center": v(24.1, -0.6) * mm, "radius": 0.02 * mm});
            skCircle(sketch, "E389", {"center": v(24.16, -0.6) * mm, "radius": 0.02 * mm});
            skCircle(sketch, "E390", {"center": v(25.54, -0.6) * mm, "radius": 0.02 * mm});
            skCircle(sketch, "E391", {"center": v(25.48, -0.6) * mm, "radius": 0.02 * mm});
            skCircle(sketch, "E392", {"center": v(24.29, -0.75) * mm, "radius": 0.03 * mm});
            skCircle(sketch, "E393", {"center": v(24.37, -0.75) * mm, "radius": 0.03 * mm});
            skCircle(sketch, "E394", {"center": v(24.46, -0.75) * mm, "radius": 0.03 * mm});
            skCircle(sketch, "E395", {"center": v(24.54, -0.75) * mm, "radius": 0.03 * mm});
            skCircle(sketch, "E396", {"center": v(24.63, -0.75) * mm, "radius": 0.03 * mm});
            skCircle(sketch, "E397", {"center": v(24.71, -0.75) * mm, "radius": 0.03 * mm});
            skCircle(sketch, "E398", {"center": v(24.8, -0.75) * mm, "radius": 0.03 * mm});
            skCircle(sketch, "E399", {"center": v(24.33, -0.82) * mm, "radius": 0.03 * mm});
            skCircle(sketch, "E400", {"center": v(24.42, -0.82) * mm, "radius": 0.03 * mm});
            skCircle(sketch, "E401", {"center": v(24.5, -0.82) * mm, "radius": 0.03 * mm});
            skCircle(sketch, "E402", {"center": v(24.59, -0.82) * mm, "radius": 0.03 * mm});
            skCircle(sketch, "E403", {"center": v(24.67, -0.82) * mm, "radius": 0.03 * mm});
            skCircle(sketch, "E404", {"center": v(24.76, -0.82) * mm, "radius": 0.03 * mm});
            skCircle(sketch, "E405", {"center": v(24.1, -0.82) * mm, "radius": 0.03 * mm});
            skCircle(sketch, "E406", {"center": v(24.18, -0.82) * mm, "radius": 0.03 * mm});
            skCircle(sketch, "E407", {"center": v(24.26, -0.82) * mm, "radius": 0.03 * mm});
            skCircle(sketch, "E408", {"center": v(25.35, -0.75) * mm, "radius": 0.03 * mm});
            skCircle(sketch, "E409", {"center": v(25.26, -0.75) * mm, "radius": 0.03 * mm});
            skCircle(sketch, "E410", {"center": v(25.18, -0.75) * mm, "radius": 0.03 * mm});
            skCircle(sketch, "E411", {"center": v(25.1, -0.75) * mm, "radius": 0.03 * mm});
            skCircle(sketch, "E412", {"center": v(25, -0.75) * mm, "radius": 0.03 * mm});
            skCircle(sketch, "E413", {"center": v(24.92, -0.75) * mm, "radius": 0.03 * mm});
            skCircle(sketch, "E414", {"center": v(25.3, -0.82) * mm, "radius": 0.03 * mm});
            skCircle(sketch, "E415", {"center": v(25.22, -0.82) * mm, "radius": 0.03 * mm});
            skCircle(sketch, "E416", {"center": v(25.14, -0.82) * mm, "radius": 0.03 * mm});
            skCircle(sketch, "E417", {"center": v(25.05, -0.82) * mm, "radius": 0.03 * mm});
            skCircle(sketch, "E418", {"center": v(24.97, -0.82) * mm, "radius": 0.03 * mm});
            skCircle(sketch, "E419", {"center": v(24.88, -0.82) * mm, "radius": 0.03 * mm});
            skCircle(sketch, "E420", {"center": v(25.42, -0.75) * mm, "radius": 0.02 * mm});
            skCircle(sketch, "E421", {"center": v(25.53, -0.82) * mm, "radius": 0.03 * mm});
            skCircle(sketch, "E422", {"center": v(25.46, -0.82) * mm, "radius": 0.03 * mm});
            skCircle(sketch, "E423", {"center": v(25.38, -0.82) * mm, "radius": 0.03 * mm});
            skCircle(sketch, "E424", {"center": v(24.1, -0.75) * mm, "radius": 0.02 * mm});
            skCircle(sketch, "E425", {"center": v(24.16, -0.75) * mm, "radius": 0.02 * mm});
            skCircle(sketch, "E426", {"center": v(25.54, -0.75) * mm, "radius": 0.02 * mm});
            skCircle(sketch, "E427", {"center": v(25.48, -0.75) * mm, "radius": 0.02 * mm});
            skLineSegment(sketch, "E428", {"start": v(25.42, 0.88) * mm, "end": v(26.8, 0.88) * mm});
            skLineSegment(sketch, "E429", {"start": v(25.42, 0.92) * mm, "end": v(26.8, 0.92) * mm});
            skLineSegment(sketch, "E430", {"start": v(26.8, 0.92) * mm, "end": v(26.8, 0.88) * mm});
            skCircle(sketch, "E431", {"center": v(24.22, -1.05) * mm, "radius": 0.02 * mm});
            skCircle(sketch, "E432", {"center": v(24.29, -0.9) * mm, "radius": 0.03 * mm});
            skCircle(sketch, "E433", {"center": v(24.37, -0.9) * mm, "radius": 0.03 * mm});
            skCircle(sketch, "E434", {"center": v(24.46, -0.9) * mm, "radius": 0.03 * mm});
            skCircle(sketch, "E435", {"center": v(24.54, -0.9) * mm, "radius": 0.03 * mm});
            skCircle(sketch, "E436", {"center": v(24.63, -0.9) * mm, "radius": 0.03 * mm});
            skCircle(sketch, "E437", {"center": v(24.71, -0.9) * mm, "radius": 0.03 * mm});
            skCircle(sketch, "E438", {"center": v(24.8, -0.9) * mm, "radius": 0.03 * mm});
            skCircle(sketch, "E439", {"center": v(24.33, -0.98) * mm, "radius": 0.03 * mm});
            skCircle(sketch, "E440", {"center": v(24.42, -0.98) * mm, "radius": 0.03 * mm});
            skCircle(sketch, "E441", {"center": v(24.5, -0.98) * mm, "radius": 0.03 * mm});
            skCircle(sketch, "E442", {"center": v(24.59, -0.98) * mm, "radius": 0.03 * mm});
            skCircle(sketch, "E443", {"center": v(24.67, -0.98) * mm, "radius": 0.03 * mm});
            skCircle(sketch, "E444", {"center": v(24.76, -0.98) * mm, "radius": 0.03 * mm});
            skArc(sketch, "E445", {"start": v(24.22, -0.92) * mm, "mid": v(24.24, -0.9) * mm, "end": v(24.22, -0.88) * mm});
            skCircle(sketch, "E446", {"center": v(24.1, -0.98) * mm, "radius": 0.03 * mm});
            skCircle(sketch, "E447", {"center": v(24.18, -0.98) * mm, "radius": 0.03 * mm});
            skCircle(sketch, "E448", {"center": v(24.26, -0.98) * mm, "radius": 0.03 * mm});
            skCircle(sketch, "E449", {"center": v(25.35, -0.9) * mm, "radius": 0.03 * mm});
            skCircle(sketch, "E450", {"center": v(25.26, -0.9) * mm, "radius": 0.03 * mm});
            skCircle(sketch, "E451", {"center": v(25.18, -0.9) * mm, "radius": 0.03 * mm});
            skCircle(sketch, "E452", {"center": v(25.1, -0.9) * mm, "radius": 0.03 * mm});
            skCircle(sketch, "E453", {"center": v(25, -0.9) * mm, "radius": 0.03 * mm});
            skCircle(sketch, "E454", {"center": v(24.92, -0.9) * mm, "radius": 0.03 * mm});
            skCircle(sketch, "E455", {"center": v(25.3, -0.98) * mm, "radius": 0.03 * mm});
            skCircle(sketch, "E456", {"center": v(25.22, -0.98) * mm, "radius": 0.03 * mm});
            skCircle(sketch, "E457", {"center": v(25.14, -0.98) * mm, "radius": 0.03 * mm});
            skCircle(sketch, "E458", {"center": v(25.05, -0.98) * mm, "radius": 0.03 * mm});
            skCircle(sketch, "E459", {"center": v(24.97, -0.98) * mm, "radius": 0.03 * mm});
            skCircle(sketch, "E460", {"center": v(24.88, -0.98) * mm, "radius": 0.03 * mm});
            skCircle(sketch, "E461", {"center": v(25.53, -0.98) * mm, "radius": 0.03 * mm});
            skCircle(sketch, "E462", {"center": v(25.46, -0.98) * mm, "radius": 0.03 * mm});
            skCircle(sketch, "E463", {"center": v(25.38, -0.98) * mm, "radius": 0.03 * mm});
            skLineSegment(sketch, "E464", {"start": v(24.22, -0.92) * mm, "end": v(22.83, -0.92) * mm});
            skLineSegment(sketch, "E465", {"start": v(24.22, -0.88) * mm, "end": v(22.83, -0.88) * mm});
            skLineSegment(sketch, "E466", {"start": v(22.83, -0.88) * mm, "end": v(22.83, -0.92) * mm});
            skCircle(sketch, "E467", {"center": v(24.29, -1.05) * mm, "radius": 0.03 * mm});
            skCircle(sketch, "E468", {"center": v(24.37, -1.05) * mm, "radius": 0.03 * mm});
            skCircle(sketch, "E469", {"center": v(24.46, -1.05) * mm, "radius": 0.03 * mm});
            skCircle(sketch, "E470", {"center": v(24.54, -1.05) * mm, "radius": 0.03 * mm});
            skCircle(sketch, "E471", {"center": v(24.63, -1.05) * mm, "radius": 0.03 * mm});
            skCircle(sketch, "E472", {"center": v(24.71, -1.05) * mm, "radius": 0.03 * mm});
            skCircle(sketch, "E473", {"center": v(24.8, -1.05) * mm, "radius": 0.03 * mm});
            skCircle(sketch, "E474", {"center": v(24.33, -1.13) * mm, "radius": 0.03 * mm});
            skCircle(sketch, "E475", {"center": v(24.42, -1.13) * mm, "radius": 0.03 * mm});
            skCircle(sketch, "E476", {"center": v(24.5, -1.13) * mm, "radius": 0.03 * mm});
            skCircle(sketch, "E477", {"center": v(24.59, -1.13) * mm, "radius": 0.03 * mm});
            skCircle(sketch, "E478", {"center": v(24.67, -1.13) * mm, "radius": 0.03 * mm});
            skCircle(sketch, "E479", {"center": v(24.76, -1.13) * mm, "radius": 0.03 * mm});
            skCircle(sketch, "E480", {"center": v(24.1, -1.13) * mm, "radius": 0.03 * mm});
            skCircle(sketch, "E481", {"center": v(24.18, -1.13) * mm, "radius": 0.03 * mm});
            skCircle(sketch, "E482", {"center": v(24.26, -1.13) * mm, "radius": 0.03 * mm});
            skCircle(sketch, "E483", {"center": v(25.35, -1.05) * mm, "radius": 0.03 * mm});
            skCircle(sketch, "E484", {"center": v(25.26, -1.05) * mm, "radius": 0.03 * mm});
            skCircle(sketch, "E485", {"center": v(25.18, -1.05) * mm, "radius": 0.03 * mm});
            skCircle(sketch, "E486", {"center": v(25.1, -1.05) * mm, "radius": 0.03 * mm});
            skCircle(sketch, "E487", {"center": v(25, -1.05) * mm, "radius": 0.03 * mm});
            skCircle(sketch, "E488", {"center": v(24.92, -1.05) * mm, "radius": 0.03 * mm});
            skCircle(sketch, "E489", {"center": v(25.3, -1.13) * mm, "radius": 0.03 * mm});
            skCircle(sketch, "E490", {"center": v(25.22, -1.13) * mm, "radius": 0.03 * mm});
            skCircle(sketch, "E491", {"center": v(25.14, -1.13) * mm, "radius": 0.03 * mm});
            skCircle(sketch, "E492", {"center": v(25.05, -1.13) * mm, "radius": 0.03 * mm});
            skCircle(sketch, "E493", {"center": v(24.97, -1.13) * mm, "radius": 0.03 * mm});
            skCircle(sketch, "E494", {"center": v(24.88, -1.13) * mm, "radius": 0.03 * mm});
            skCircle(sketch, "E495", {"center": v(25.42, -1.05) * mm, "radius": 0.02 * mm});
            skCircle(sketch, "E496", {"center": v(25.53, -1.13) * mm, "radius": 0.03 * mm});
            skCircle(sketch, "E497", {"center": v(25.46, -1.13) * mm, "radius": 0.03 * mm});
            skCircle(sketch, "E498", {"center": v(25.38, -1.13) * mm, "radius": 0.03 * mm});
            skCircle(sketch, "E499", {"center": v(24.1, -1.05) * mm, "radius": 0.02 * mm});
            skCircle(sketch, "E500", {"center": v(24.16, -1.05) * mm, "radius": 0.02 * mm});
            skCircle(sketch, "E501", {"center": v(25.54, -1.05) * mm, "radius": 0.02 * mm});
            skCircle(sketch, "E502", {"center": v(25.48, -1.05) * mm, "radius": 0.02 * mm});
            skArc(sketch, "E503", {"start": v(25.42, -0.88) * mm, "mid": v(25.4, -0.9) * mm, "end": v(25.42, -0.92) * mm});
            skLineSegment(sketch, "E504", {"start": v(25.42, -0.92) * mm, "end": v(26.8, -0.92) * mm});
            skLineSegment(sketch, "E505", {"start": v(25.42, -0.88) * mm, "end": v(26.8, -0.88) * mm});
            skLineSegment(sketch, "E506", {"start": v(26.8, -0.88) * mm, "end": v(26.8, -0.92) * mm});
            skLineSegment(sketch, "E507", {"start": v(24.22, 0.92) * mm, "end": v(24.22, 0.88) * mm});
            skLineSegment(sketch, "E508", {"start": v(24.24, 0.92) * mm, "end": v(24.24, 0.88) * mm});
            skLineSegment(sketch, "E509", {"start": v(25.42, 0.92) * mm, "end": v(25.42, 0.88) * mm});
            skLineSegment(sketch, "E510", {"start": v(25.4, 0.92) * mm, "end": v(25.4, 0.88) * mm});
            skLineSegment(sketch, "E511", {"start": v(24.24, 0.92) * mm, "end": v(25.4, 0.92) * mm});
            skLineSegment(sketch, "E512", {"start": v(24.24, 0.88) * mm, "end": v(25.4, 0.88) * mm});
            skLineSegment(sketch, "E513", {"start": v(27.3, 1.42) * mm, "end": v(22.33, 1.42) * mm});
            skLineSegment(sketch, "E514", {"start": v(27.3, -1.42) * mm, "end": v(22.33, -1.42) * mm});
            skLineSegment(sketch, "E515", {"start": v(22.33, 1.42) * mm, "end": v(22.33, -1.42) * mm});
            skLineSegment(sketch, "E516", {"start": v(27.3, 1.42) * mm, "end": v(27.3, -1.42) * mm});
            skSolve(sketch);
        }
        {
            var Q0;
            Q0=makeQuery(id+"F0.imprint","IMPRINT",FACE,{"disambiguationData":[TD([[makeQuery(id+"F0.imprint","IMPRINT",EDGE,{"derivedFrom":sQuery(id+"F0.wireOp",EDGE,"E0")}),1.0]])]});
            extrude(context, id + "F1", {"entities" : qUnion([Q0]), "depth" : .25 * mm});
        }
    });
